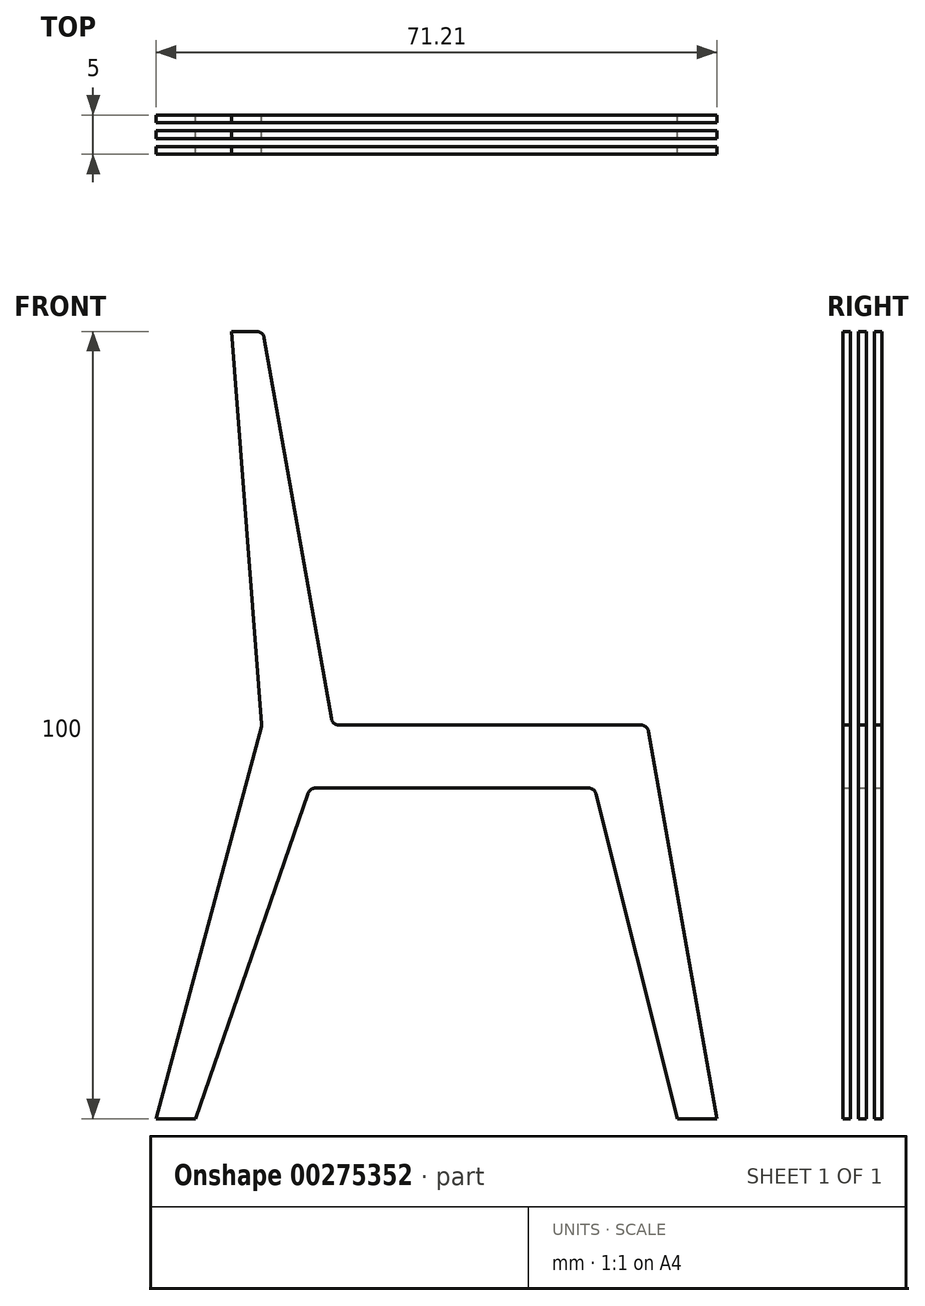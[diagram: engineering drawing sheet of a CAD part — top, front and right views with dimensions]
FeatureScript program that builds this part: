
annotation { "Feature Type Name" : "Feature", "Feature Type Description" : "" }
export const myFeature = defineFeature(function(context is Context, id is Id, definition is map)
    precondition{}
    {
        {
            assignVariable(context, id + "F0", {"name" : "ES", "anyValue" : 1});
        }
        {
            var Q0;
            Q0=qCreatedBy(makeId("Front.planeOp"),FACE);
            var sketch = newSketch(context, id + "F1", { "sketchPlane" : qUnion([Q0])});
            skLineSegment(sketch, "E0", {"start": v(-37.61, -50) * mm, "end": v(-24.26, -0.16) * mm});
            skLineSegment(sketch, "E1", {"start": v(-14.37, 0) * mm, "end": v(23.95, 0) * mm});
            skLineSegment(sketch, "E2", {"start": v(24.93, -0.83) * mm, "end": v(33.6, -50) * mm});
            skLineSegment(sketch, "E3", {"start": v(33.6, -50) * mm, "end": v(28.6, -50) * mm});
            skLineSegment(sketch, "E4", {"start": v(28.6, -50) * mm, "end": v(18.26, -8.76) * mm});
            skLineSegment(sketch, "E5", {"start": v(17.3, -8) * mm, "end": v(-17.36, -8) * mm});
            skLineSegment(sketch, "E6", {"start": v(-18.3, -8.67) * mm, "end": v(-32.61, -50) * mm});
            skLineSegment(sketch, "E7", {"start": v(-32.61, -50) * mm, "end": v(-37.61, -50) * mm});
            skPoint(sketch, "E8", {"position": v(0, -8) * mm});
            skLineSegment(sketch, "E9", {"start": v(-24.23, 0.17) * mm, "end": v(-28.03, 50) * mm});
            skLineSegment(sketch, "E10", {"start": v(-28.03, 50) * mm, "end": v(-24.87, 50) * mm});
            skLineSegment(sketch, "E11", {"start": v(-23.88, 49.17) * mm, "end": v(-15.36, 0.83) * mm});
            skPoint(sketch, "E12.visualSharp", {"position": v(-18.07, -8) * mm});
            skArc(sketch, "E12.filletArc", {"start": v(-17.36, -8) * mm, "mid": v(-17.94, -8.19) * mm, "end": v(-18.3, -8.67) * mm});
            skPoint(sketch, "E13.visualSharp", {"position": v(18.07, -8) * mm});
            skArc(sketch, "E13.filletArc", {"start": v(18.26, -8.76) * mm, "mid": v(17.9, -8.21) * mm, "end": v(17.3, -8) * mm});
            skPoint(sketch, "E14.visualSharp", {"position": v(24.79, 0) * mm});
            skArc(sketch, "E14.filletArc", {"start": v(24.93, -0.83) * mm, "mid": v(24.6, -0.23) * mm, "end": v(23.95, 0) * mm});
            skPoint(sketch, "E15.visualSharp", {"position": v(-15.21, 0) * mm});
            skArc(sketch, "E15.filletArc", {"start": v(-15.36, 0.83) * mm, "mid": v(-15.02, 0.23) * mm, "end": v(-14.37, 0) * mm});
            skPoint(sketch, "E16.visualSharp", {"position": v(-24.03, 50) * mm});
            skArc(sketch, "E16.filletArc", {"start": v(-23.88, 49.17) * mm, "mid": v(-24.23, 49.77) * mm, "end": v(-24.87, 50) * mm});
            skPoint(sketch, "E17.visualSharp", {"position": v(-24.21, 0) * mm});
            skArc(sketch, "E17.filletArc", {"start": v(-24.26, -0.16) * mm, "mid": v(-24.23, 0) * mm, "end": v(-24.23, 0.17) * mm});
            skLineSegment(sketch, "E18", {"start": v(24.6, -0.23) * mm, "end": v(17.9, -8.2) * mm, "construction": true});
            skSolve(sketch);
        }
        {
            var Q0;
            Q0=makeQuery(id+"F1.imprint","IMPRINT",FACE,{"disambiguationData":[TD([[makeQuery(id+"F1.imprint","IMPRINT",EDGE,{"derivedFrom":sQuery(id+"F1.wireOp",EDGE,"E0")}),-1.0]])]});
            extrude(context, id + "F2", {"entities" : qUnion([Q0]), "depth" : (getVariable(context, 'ES')) * mm, "offsetDistance" : 25 * mm});
        }
        {
            var Q0;
            Q0=makeQuery(id+"F2.opExtrude","SWEPT_BODY",BODY,{"disambiguationData":[OSD([sQuery(id+"F1.wireOp",EDGE,"E0"),sQuery(id+"F1.wireOp",EDGE,"E1"),sQuery(id+"F1.wireOp",EDGE,"E2"),sQuery(id+"F1.wireOp",EDGE,"E3"),sQuery(id+"F1.wireOp",EDGE,"E4"),sQuery(id+"F1.wireOp",EDGE,"E5"),sQuery(id+"F1.wireOp",EDGE,"E6"),sQuery(id+"F1.wireOp",EDGE,"E7"),sQuery(id+"F1.wireOp",EDGE,"E9"),sQuery(id+"F1.wireOp",EDGE,"E10"),sQuery(id+"F1.wireOp",EDGE,"E11"),sQuery(id+"F1.wireOp",EDGE,"E12.filletArc"),sQuery(id+"F1.wireOp",EDGE,"E13.filletArc"),sQuery(id+"F1.wireOp",EDGE,"E14.filletArc"),sQuery(id+"F1.wireOp",EDGE,"E15.filletArc"),sQuery(id+"F1.wireOp",EDGE,"E16.filletArc"),sQuery(id+"F1.wireOp",EDGE,"E17.filletArc")])]});
            transform(context, id + "F3", {"entities" : qUnion([Q0]), "transformType" : TransformType.TRANSLATION_3D, "dx" : 0 * mm, "dy" : (getVariable(context, 'ES') * 2) * mm, "dz" : 0 * mm, "makeCopy" : true});
        }
        {
            var Q0;
            Q0=makeQuery(id+"F3.opPattern","COPY",BODY,{"derivedFrom":makeQuery(id+"F2.opExtrude","SWEPT_BODY",BODY,{"disambiguationData":[OSD([sQuery(id+"F1.wireOp",EDGE,"E0"),sQuery(id+"F1.wireOp",EDGE,"E1"),sQuery(id+"F1.wireOp",EDGE,"E2"),sQuery(id+"F1.wireOp",EDGE,"E3"),sQuery(id+"F1.wireOp",EDGE,"E4"),sQuery(id+"F1.wireOp",EDGE,"E5"),sQuery(id+"F1.wireOp",EDGE,"E6"),sQuery(id+"F1.wireOp",EDGE,"E7"),sQuery(id+"F1.wireOp",EDGE,"E9"),sQuery(id+"F1.wireOp",EDGE,"E10"),sQuery(id+"F1.wireOp",EDGE,"E11"),sQuery(id+"F1.wireOp",EDGE,"E12.filletArc"),sQuery(id+"F1.wireOp",EDGE,"E13.filletArc"),sQuery(id+"F1.wireOp",EDGE,"E14.filletArc"),sQuery(id+"F1.wireOp",EDGE,"E15.filletArc"),sQuery(id+"F1.wireOp",EDGE,"E16.filletArc"),sQuery(id+"F1.wireOp",EDGE,"E17.filletArc")])]}),"instanceName":"1"});
            transform(context, id + "F4", {"entities" : qUnion([Q0]), "transformType" : TransformType.TRANSLATION_3D, "dx" : 0 * mm, "dy" : (getVariable(context, 'ES') * 2) * mm, "dz" : 0 * mm, "makeCopy" : true});
        }
    });
